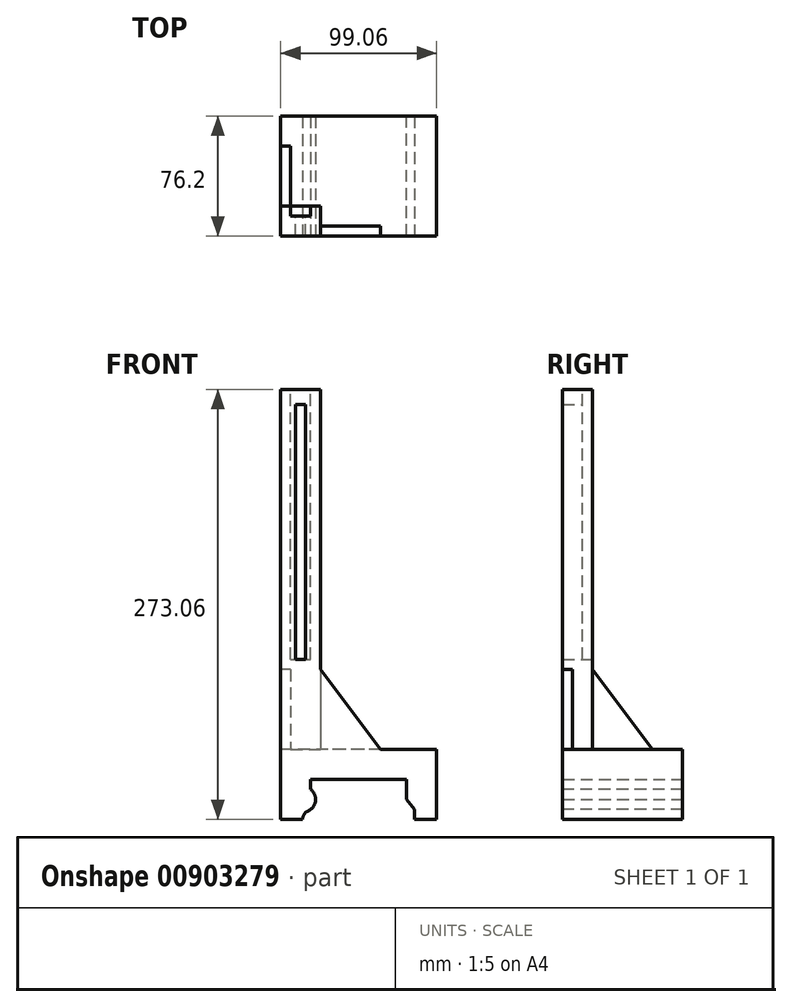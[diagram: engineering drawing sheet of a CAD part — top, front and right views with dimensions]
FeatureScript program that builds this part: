
annotation { "Feature Type Name" : "Feature", "Feature Type Description" : "" }
export const myFeature = defineFeature(function(context is Context, id is Id, definition is map)
    precondition{}
    {
        {
            var Q0;
            Q0=qCreatedBy(makeId("Front.planeOp"),FACE);
            var sketch = newSketch(context, id + "F0", { "sketchPlane" : qUnion([Q0])});
            skLineSegment(sketch, "E0.bottom", {"start": v(49.53, -22.23) * mm, "end": v(-49.53, -22.23) * mm});
            skLineSegment(sketch, "E0.top", {"start": v(49.53, 22.23) * mm, "end": v(-49.53, 22.23) * mm});
            skLineSegment(sketch, "E0.left", {"start": v(49.53, -22.23) * mm, "end": v(49.53, 22.23) * mm});
            skLineSegment(sketch, "E0.right", {"start": v(-49.53, -22.23) * mm, "end": v(-49.53, 22.22) * mm});
            skPoint(sketch, "E0.middle", {"position": v(0, 0) * mm});
            skLineSegment(sketch, "E1.bottom", {"start": v(30.48, -47.63) * mm, "end": v(-30.48, -47.63) * mm});
            skLineSegment(sketch, "E1.top", {"start": v(30.48, 3.18) * mm, "end": v(-30.48, 3.18) * mm});
            skLineSegment(sketch, "E1.left", {"start": v(30.48, -47.63) * mm, "end": v(30.48, 3.18) * mm});
            skLineSegment(sketch, "E1.right", {"start": v(-30.48, -47.63) * mm, "end": v(-30.48, 3.18) * mm});
            skPoint(sketch, "E1.middle", {"position": v(0, -22.23) * mm});
            skSolve(sketch);
        }
        {
            var Q0;
            Q0=makeQuery(id+"F0.imprint","IMPRINT",FACE,{"disambiguationData":[TD([[makeQuery(id+"F0.imprint","IMPRINT",EDGE,{"derivedFrom":sQuery(id+"F0.wireOp",EDGE,"E0.top")}),1.0]])]});
            extrude(context, id + "F1", {"entities" : qUnion([Q0]), "endBound" : BoundingType.SYMMETRIC, "depth" : 76.2 * mm, "offsetDistance" : 25.4 * mm});
        }
        {
            var Q0;
            Q0=qCreatedBy(makeId("Front.planeOp"),FACE);
            var sketch = newSketch(context, id + "F2", { "sketchPlane" : qUnion([Q0])});
            skLineSegment(sketch, "E2.bottom", {"start": v(35.56, -36.92) * mm, "end": v(-35.56, -36.92) * mm});
            skLineSegment(sketch, "E2.top", {"start": v(35.56, -9.52) * mm, "end": v(-35.56, -9.53) * mm});
            skLineSegment(sketch, "E2.left", {"start": v(35.56, -36.92) * mm, "end": v(35.56, -9.53) * mm});
            skLineSegment(sketch, "E2.right", {"start": v(-35.56, -36.92) * mm, "end": v(-35.56, -9.53) * mm});
            skPoint(sketch, "E2.middle", {"position": v(0, -23.22) * mm});
            skSolve(sketch);
        }
        {
            var Q0;
            Q0=makeQuery(id+"F2.imprint","IMPRINT",FACE,{"disambiguationData":[TD([[makeQuery(id+"F2.imprint","IMPRINT",EDGE,{"derivedFrom":sQuery(id+"F2.wireOp",EDGE,"E2.bottom")}),-1.0]])]});
            extrude(context, id + "F3", {"entities" : qUnion([Q0]), "operationType" : NewBodyOperationType.REMOVE, "endBound" : BoundingType.SYMMETRIC, "oppositeDirection" : true, "depth" : 101.6 * mm, "offsetDistance" : 25.4 * mm});
        }
        {
            var Q0;
            Q0=makeQuery(id+"F1.opExtrude","SWEPT_FACE",FACE,{"disambiguationData":[OSD([sQuery(id+"F0.wireOp",EDGE,"E0.top")])]});
            var sketch = newSketch(context, id + "F4", { "sketchPlane" : qUnion([Q0])});
            skLineSegment(sketch, "E3.bottom", {"start": v(-49.53, -38.1) * mm, "end": v(-24.13, -38.1) * mm});
            skLineSegment(sketch, "E3.top", {"start": v(-49.53, -19.05) * mm, "end": v(-24.13, -19.05) * mm});
            skLineSegment(sketch, "E3.left", {"start": v(-49.53, -38.1) * mm, "end": v(-49.53, -19.05) * mm});
            skLineSegment(sketch, "E3.right", {"start": v(-24.13, -38.1) * mm, "end": v(-24.13, -19.05) * mm});
            skSolve(sketch);
        }
        {
            var Q0;
            Q0 = qSketchRegion(id + "F4", true);
            extrude(context, id + "F5", {"entities" : qUnion([Q0]), "operationType" : NewBodyOperationType.ADD, "depth" : 228.6 * mm, "offsetDistance" : 25.4 * mm});
        }
        {
            var Q0;
            Q0=makeQuery(id+"F5.boolean.opBoolean","MERGE",FACE,{"derivedFrom":[makeQuery(id+"F1.opExtrude","CAP_FACE",FACE,{"disambiguationData":[OSD([sQuery(id+"F0.wireOp",EDGE,"E0.bottom"),sQuery(id+"F0.wireOp",EDGE,"E0.top"),sQuery(id+"F0.wireOp",EDGE,"E0.left"),sQuery(id+"F0.wireOp",EDGE,"E0.right"),sQuery(id+"F0.wireOp",EDGE,"E1.top"),sQuery(id+"F0.wireOp",EDGE,"E1.left"),sQuery(id+"F0.wireOp",EDGE,"E1.right")])],"isStart":false}),makeQuery(id+"F5.opExtrude","SWEPT_FACE",FACE,{"disambiguationData":[OSD([sQuery(id+"F4.wireOp",EDGE,"E3.bottom")])]})]});
            var sketch = newSketch(context, id + "F6", { "sketchPlane" : qUnion([Q0])});
            skLineSegment(sketch, "E4", {"start": v(-24.13, 22.23) * mm, "end": v(13.97, 22.23) * mm});
            skLineSegment(sketch, "E5", {"start": v(-24.13, 22.23) * mm, "end": v(-24.13, 73.03) * mm});
            skLineSegment(sketch, "E6", {"start": v(-24.13, 73.03) * mm, "end": v(13.97, 22.23) * mm});
            skSolve(sketch);
        }
        {
            var Q0;
            Q0 = qSketchRegion(id + "F6", true);
            extrude(context, id + "F7", {"entities" : qUnion([Q0]), "operationType" : NewBodyOperationType.ADD, "oppositeDirection" : true, "depth" : 6.35 * mm, "offsetDistance" : 25.4 * mm});
        }
        {
            var Q0;
            Q0=makeQuery(id+"F5.opExtrude","SWEPT_FACE",FACE,{"disambiguationData":[OSD([sQuery(id+"F4.wireOp",EDGE,"E3.top")])]});
            var sketch = newSketch(context, id + "F8", { "sketchPlane" : qUnion([Q0])});
            skLineSegment(sketch, "E7.bottom", {"start": v(43.18, 79.38) * mm, "end": v(30.48, 79.38) * mm});
            skLineSegment(sketch, "E7.top", {"start": v(43.18, 244.48) * mm, "end": v(30.48, 244.48) * mm});
            skLineSegment(sketch, "E7.left", {"start": v(43.18, 79.38) * mm, "end": v(43.18, 244.47) * mm});
            skLineSegment(sketch, "E7.right", {"start": v(30.48, 79.38) * mm, "end": v(30.48, 244.48) * mm});
            skPoint(sketch, "E7.middle", {"position": v(36.83, 161.93) * mm});
            skPoint(sketch, "E8.bottom.end.orphan", {"position": v(33.65, 82.55) * mm});
            skPoint(sketch, "E8.left.start.orphan", {"position": v(40, 82.55) * mm});
            skPoint(sketch, "E8.top.end.orphan", {"position": v(33.65, 241.3) * mm});
            skPoint(sketch, "E8.top.start.orphan", {"position": v(40, 241.3) * mm});
            skSolve(sketch);
        }
        {
            var Q0;
            Q0=makeQuery(id+"F8.imprint","IMPRINT",FACE,{"disambiguationData":[TD([[makeQuery(id+"F8.imprint","IMPRINT",EDGE,{"derivedFrom":sQuery(id+"F8.wireOp",EDGE,"E7.bottom")}),-1.0]])]});
            extrude(context, id + "F9", {"entities" : qUnion([Q0]), "operationType" : NewBodyOperationType.REMOVE, "oppositeDirection" : true, "depth" : 6.35 * mm, "offsetDistance" : 25.4 * mm});
        }
        {
            var Q0;
            Q0=qCreatedBy(makeId("Front.planeOp"),FACE);
            var sketch = newSketch(context, id + "F10", { "sketchPlane" : qUnion([Q0])});
            skLineSegment(sketch, "E9.bottom", {"start": v(-33.66, 79.38) * mm, "end": v(-40, 79.38) * mm});
            skLineSegment(sketch, "E9.top", {"start": v(-33.66, 241.3) * mm, "end": v(-40, 241.3) * mm});
            skLineSegment(sketch, "E9.left", {"start": v(-33.66, 79.38) * mm, "end": v(-33.66, 241.3) * mm});
            skLineSegment(sketch, "E9.right", {"start": v(-40, 79.38) * mm, "end": v(-40, 241.3) * mm});
            skSolve(sketch);
        }
        {
            var Q0;
            Q0 = qSketchRegion(id + "F10", true);
            extrude(context, id + "F11", {"entities" : qUnion([Q0]), "operationType" : NewBodyOperationType.REMOVE, "depth" : 127 * mm, "offsetDistance" : 25.4 * mm});
        }
        {
            var Q0;
            Q0=makeQuery(id+"F5.boolean.opBoolean","MERGE",FACE,{"derivedFrom":[makeQuery(id+"F1.opExtrude","SWEPT_FACE",FACE,{"disambiguationData":[OSD([sQuery(id+"F0.wireOp",EDGE,"E0.right")])]}),makeQuery(id+"F5.opExtrude","SWEPT_FACE",FACE,{"disambiguationData":[OSD([sQuery(id+"F4.wireOp",EDGE,"E3.left")])]})]});
            var sketch = newSketch(context, id + "F12", { "sketchPlane" : qUnion([Q0])});
            skLineSegment(sketch, "E10", {"start": v(19.05, 22.23) * mm, "end": v(-19.05, 22.23) * mm});
            skLineSegment(sketch, "E11", {"start": v(19.05, 22.23) * mm, "end": v(19.05, 73.03) * mm});
            skLineSegment(sketch, "E12", {"start": v(-19.05, 22.22) * mm, "end": v(19.05, 73.03) * mm});
            skSolve(sketch);
        }
        {
            var Q0;
            Q0 = qSketchRegion(id + "F12", true);
            extrude(context, id + "F13", {"entities" : qUnion([Q0]), "operationType" : NewBodyOperationType.ADD, "oppositeDirection" : true, "depth" : 6.35 * mm, "offsetDistance" : 25.4 * mm});
        }
        {
            var Q0;
            Q0=makeQuery(id+"F5.opExtrude","SWEPT_FACE",FACE,{"disambiguationData":[OSD([sQuery(id+"F4.wireOp",EDGE,"E3.top")])]});
            var sketch = newSketch(context, id + "F14", { "sketchPlane" : qUnion([Q0])});
            skLineSegment(sketch, "E13.bottom", {"start": v(43.18, 236.82) * mm, "end": v(30.48, 236.82) * mm});
            skLineSegment(sketch, "E13.top", {"start": v(43.18, 252.13) * mm, "end": v(30.48, 252.13) * mm});
            skLineSegment(sketch, "E13.left", {"start": v(43.18, 236.82) * mm, "end": v(43.18, 252.13) * mm});
            skLineSegment(sketch, "E13.right", {"start": v(30.48, 236.82) * mm, "end": v(30.48, 252.13) * mm});
            skPoint(sketch, "E13.middle", {"position": v(36.83, 244.48) * mm});
            skSolve(sketch);
        }
        {
            var Q0;
            Q0 = qSketchRegion(id + "F14", true);
            extrude(context, id + "F15", {"entities" : qUnion([Q0]), "operationType" : NewBodyOperationType.REMOVE, "oppositeDirection" : true, "depth" : 6.35 * mm, "offsetDistance" : 25.4 * mm});
        }
        {
            var Q0;
            Q0=makeQuery(id+"F7.boolean.opBoolean","MERGE",FACE,{"derivedFrom":[makeQuery(id+"F5.boolean.opBoolean","MERGE",FACE,{"derivedFrom":[makeQuery(id+"F1.opExtrude","CAP_FACE",FACE,{"disambiguationData":[OSD([sQuery(id+"F0.wireOp",EDGE,"E0.bottom"),sQuery(id+"F0.wireOp",EDGE,"E0.top"),sQuery(id+"F0.wireOp",EDGE,"E0.left"),sQuery(id+"F0.wireOp",EDGE,"E0.right"),sQuery(id+"F0.wireOp",EDGE,"E1.top"),sQuery(id+"F0.wireOp",EDGE,"E1.left"),sQuery(id+"F0.wireOp",EDGE,"E1.right")])],"isStart":false}),makeQuery(id+"F5.opExtrude","SWEPT_FACE",FACE,{"disambiguationData":[OSD([sQuery(id+"F4.wireOp",EDGE,"E3.bottom")])]})]}),makeQuery(id+"F7.opExtrude","CAP_FACE",FACE,{"disambiguationData":[OSD([sQuery(id+"F6.wireOp",EDGE,"E4"),sQuery(id+"F6.wireOp",EDGE,"E5"),sQuery(id+"F6.wireOp",EDGE,"E6")])],"isStart":true})]});
            var sketch = newSketch(context, id + "F16", { "sketchPlane" : qUnion([Q0])});
            skCircle(sketch, "E14", {"center": v(-35.56, -9.53) * mm, "radius": 8.13 * mm});
            skSolve(sketch);
        }
        {
            var Q0;
            Q0 = qSketchRegion(id + "F16", true);
            extrude(context, id + "F17", {"entities" : qUnion([Q0]), "operationType" : NewBodyOperationType.ADD, "oppositeDirection" : true, "depth" : 76.2 * mm, "offsetDistance" : 25.4 * mm});
        }
        {
            var Q0;
            Q0=makeQuery(id+"F17.boolean.opBoolean","INTERSECT",EDGE,{"derivedFrom":[makeQuery(id+"F3.boolean.opBoolean","COPY",FACE,{"derivedFrom":makeQuery(id+"F3.opExtrude","SWEPT_FACE",FACE,{"disambiguationData":[OSD([sQuery(id+"F2.wireOp",EDGE,"E2.right")])]})}),makeQuery(id+"F17.opExtrude","SWEPT_FACE",FACE,{"disambiguationData":[OSD([sQuery(id+"F16.wireOp",EDGE,"E14")])]})]});
            fillet(context, id + "F18", {"entities" : qUnion([Q0]), "radius" : 5.08 * mm, "tangentPropagation" : true, "allowEdgeOverflow" : false});
        }
        {
            var Q0;
            Q0=makeQuery(id+"F17.boolean.opBoolean","MERGE",FACE,{"derivedFrom":[makeQuery(id+"F7.boolean.opBoolean","MERGE",FACE,{"derivedFrom":[makeQuery(id+"F5.boolean.opBoolean","MERGE",FACE,{"derivedFrom":[makeQuery(id+"F1.opExtrude","CAP_FACE",FACE,{"disambiguationData":[OSD([sQuery(id+"F0.wireOp",EDGE,"E0.bottom"),sQuery(id+"F0.wireOp",EDGE,"E0.top"),sQuery(id+"F0.wireOp",EDGE,"E0.left"),sQuery(id+"F0.wireOp",EDGE,"E0.right"),sQuery(id+"F0.wireOp",EDGE,"E1.top"),sQuery(id+"F0.wireOp",EDGE,"E1.left"),sQuery(id+"F0.wireOp",EDGE,"E1.right")])],"isStart":false}),makeQuery(id+"F5.opExtrude","SWEPT_FACE",FACE,{"disambiguationData":[OSD([sQuery(id+"F4.wireOp",EDGE,"E3.bottom")])]})]}),makeQuery(id+"F7.opExtrude","CAP_FACE",FACE,{"disambiguationData":[OSD([sQuery(id+"F6.wireOp",EDGE,"E4"),sQuery(id+"F6.wireOp",EDGE,"E5"),sQuery(id+"F6.wireOp",EDGE,"E6")])],"isStart":true})]}),makeQuery(id+"F17.opExtrude","CAP_FACE",FACE,{"disambiguationData":[OSD([sQuery(id+"F16.wireOp",EDGE,"E14")])],"isStart":true})]});
            var sketch = newSketch(context, id + "F19", { "sketchPlane" : qUnion([Q0])});
            skLineSegment(sketch, "E15", {"start": v(30.48, -9.52) * mm, "end": v(35.56, -9.52) * mm});
            skLineSegment(sketch, "E16", {"start": v(35.56, -9.52) * mm, "end": v(35.56, -15.88) * mm});
            skLineSegment(sketch, "E17", {"start": v(35.56, -15.88) * mm, "end": v(30.48, -9.53) * mm});
            skSolve(sketch);
        }
        {
            var Q0;
            Q0 = qSketchRegion(id + "F19", true);
            extrude(context, id + "F20", {"entities" : qUnion([Q0]), "operationType" : NewBodyOperationType.ADD, "oppositeDirection" : true, "depth" : 76.2 * mm, "offsetDistance" : 25.4 * mm});
        }
    });
